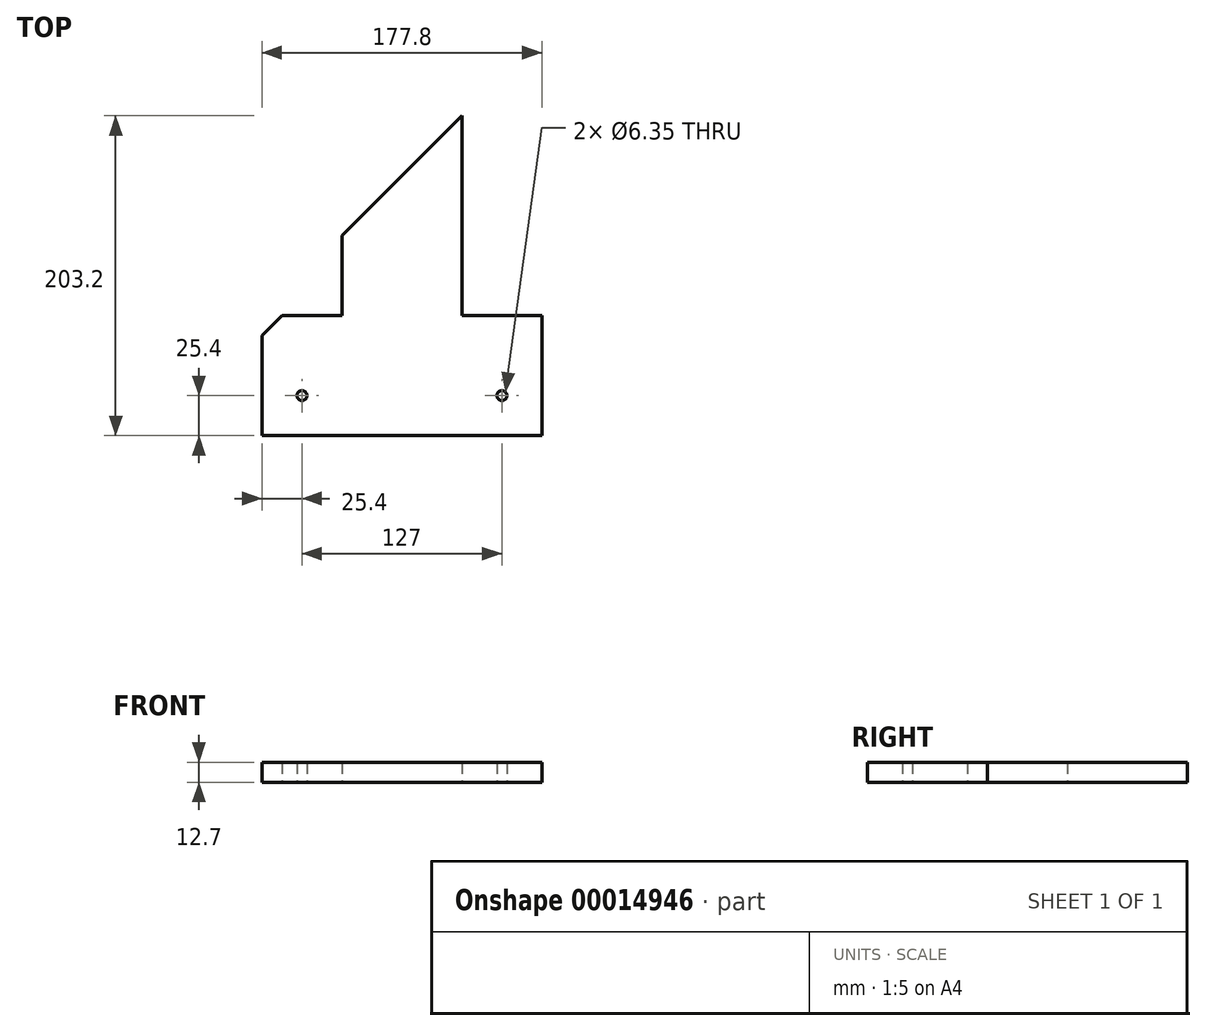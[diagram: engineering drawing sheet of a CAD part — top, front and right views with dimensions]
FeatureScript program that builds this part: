
annotation { "Feature Type Name" : "Feature", "Feature Type Description" : "" }
export const myFeature = defineFeature(function(context is Context, id is Id, definition is map)
    precondition{}
    {
        {
            var Q0;
            Q0=qCreatedBy(makeId("Top.planeOp"),FACE);
            var sketch = newSketch(context, id + "F0", { "sketchPlane" : qUnion([Q0])});
            skLineSegment(sketch, "E0.bottom", {"start": v(0, 0) * mm, "end": v(177.8, 0) * mm});
            skLineSegment(sketch, "E0.top", {"start": v(0, 76.2) * mm, "end": v(177.8, 76.2) * mm});
            skLineSegment(sketch, "E0.left", {"start": v(0, 0) * mm, "end": v(0, 76.2) * mm});
            skLineSegment(sketch, "E0.right", {"start": v(177.8, 0) * mm, "end": v(177.8, 76.2) * mm});
            skCircle(sketch, "E1", {"center": v(25.4, 25.4) * mm, "radius": 3.18 * mm});
            skCircle(sketch, "E2", {"center": v(152.4, 25.4) * mm, "radius": 3.18 * mm});
            skPoint(sketch, "E3", {"position": v(152.4, 161.92) * mm});
            skLineSegment(sketch, "E4.bottom", {"start": v(127, 76.2) * mm, "end": v(177.8, 76.2) * mm});
            skLineSegment(sketch, "E4.top", {"start": v(127, 203.2) * mm, "end": v(177.8, 203.2) * mm});
            skLineSegment(sketch, "E4.left", {"start": v(177.8, 76.2) * mm, "end": v(177.8, 203.2) * mm});
            skLineSegment(sketch, "E4.right", {"start": v(127, 76.2) * mm, "end": v(127, 203.2) * mm});
            skCircle(sketch, "E5", {"center": v(152.4, 161.92) * mm, "radius": 19.05 * mm});
            skLineSegment(sketch, "E6", {"start": v(127, 203.2) * mm, "end": v(0, 76.2) * mm});
            skLineSegment(sketch, "E7", {"start": v(0, 63.5) * mm, "end": v(12.7, 76.2) * mm});
            skLineSegment(sketch, "E8", {"start": v(50.8, 76.2) * mm, "end": v(50.8, 127) * mm});
            skSolve(sketch);
        }
        {
            var Q0;
            Q0=makeQuery(id+"F0.imprint","IMPRINT",FACE,{"disambiguationData":[TD([[makeQuery(id+"F0.imprint","IMPRINT",EDGE,{"derivedFrom":sQuery(id+"F0.wireOp",EDGE,"E0.bottom")}),1.0]])]});
            var Q1;
            Q1=makeQuery(id+"F0.imprint","IMPRINT",FACE,{"disambiguationData":[TD([[makeQuery(id+"F0.imprint","IMPRINT",EDGE,{"derivedFrom":sQuery(id+"F0.wireOp",EDGE,"E4.bottom")}),1.0]])]});
            var Q2;
            {var subQ2=sQuery(id+"F0.wireOp",EDGE,"E4.right");Q2=makeQuery(id+"F0.imprint","IMPRINT",FACE,{"disambiguationData":[TD([[makeQuery(id+"F0.imprint","IMPRINT",EDGE,{"derivedFrom":subQ2}),1.0]])]});}
            extrude(context, id + "F1", {"entities" : qUnion([Q0, Q1, Q2]), "depth" : 12.7 * mm});
        }
    });
